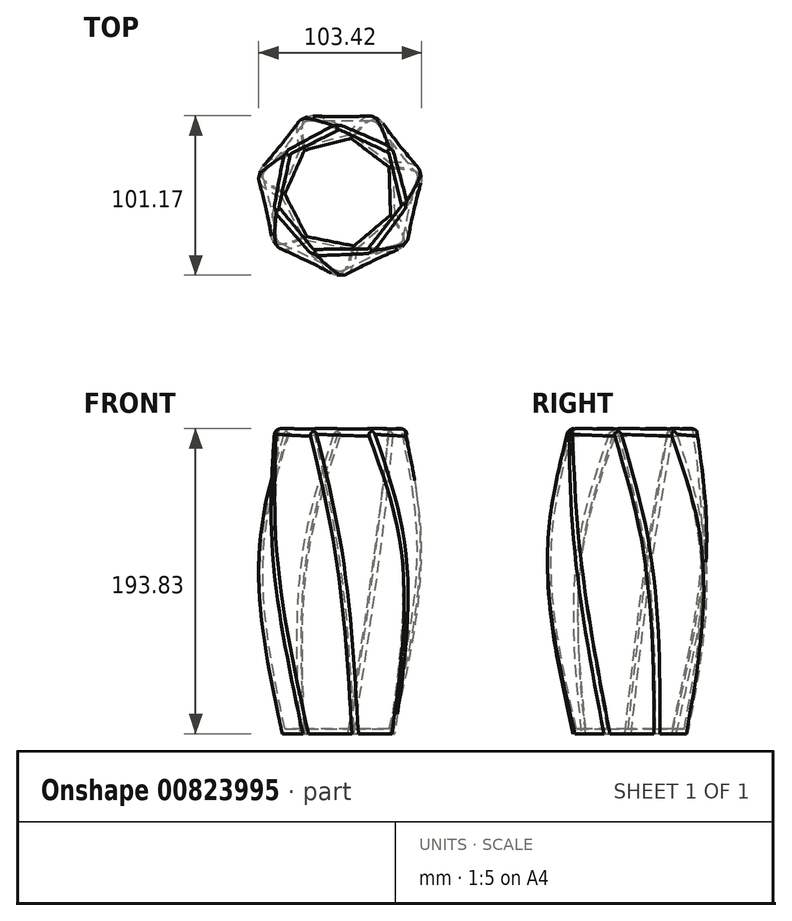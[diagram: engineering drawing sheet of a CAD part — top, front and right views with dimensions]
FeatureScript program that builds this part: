
annotation { "Feature Type Name" : "Feature", "Feature Type Description" : "" }
export const myFeature = defineFeature(function(context is Context, id is Id, definition is map)
    precondition{}
    {
        {
            var Q0;
            Q0=qCreatedBy(makeId("Top.planeOp"),FACE);
            var sketch = newSketch(context, id + "F0", { "sketchPlane" : qUnion([Q0])});
            skCircle(sketch, "E0.cCircle", {"center": v(0, 0) * mm, "radius": 34.1 * mm, "construction": true});
            skLineSegment(sketch, "E0.0", {"start": v(34.68, -15.16) * mm, "end": v(9.77, -36.56) * mm});
            skLineSegment(sketch, "E0.1", {"start": v(9.77, -36.56) * mm, "end": v(-22.5, -30.44) * mm});
            skLineSegment(sketch, "E0.2", {"start": v(-22.5, -30.44) * mm, "end": v(-37.82, -1.4) * mm});
            skLineSegment(sketch, "E0.3", {"start": v(-37.82, -1.4) * mm, "end": v(-24.67, 28.7) * mm});
            skLineSegment(sketch, "E0.4", {"start": v(-24.67, 28.7) * mm, "end": v(7.06, 37.18) * mm});
            skLineSegment(sketch, "E0.5", {"start": v(7.06, 37.18) * mm, "end": v(33.47, 17.66) * mm});
            skLineSegment(sketch, "E0.6", {"start": v(33.47, 17.66) * mm, "end": v(34.68, -15.16) * mm});
            skPoint(sketch, "E0.0.midPoint", {"position": v(22.23, -25.86) * mm});
            skSolve(sketch);
        }
        {
            var Q0;
            Q0=qCreatedBy(makeId("Top.planeOp"),FACE);
            cPlane(context, id + "F1", {"entities" : qUnion([Q0]), "cplaneType" : CPlaneType.OFFSET, "offset" : 127.3 * mm, "width" : 150 * mm, "height" : 150 * mm});
        }
        {
            var Q0;
            Q0=qCreatedBy(id+"F1.planeOp",FACE);
            var sketch = newSketch(context, id + "F2", { "sketchPlane" : qUnion([Q0])});
            skCircle(sketch, "E1.cCircle", {"center": v(0, 0) * mm, "radius": 47.61 * mm, "construction": true});
            skLineSegment(sketch, "E1.0", {"start": v(52.11, 8.77) * mm, "end": v(39.35, -35.27) * mm});
            skLineSegment(sketch, "E1.1", {"start": v(39.35, -35.27) * mm, "end": v(-3.04, -52.76) * mm});
            skLineSegment(sketch, "E1.2", {"start": v(-3.04, -52.76) * mm, "end": v(-43.15, -30.52) * mm});
            skLineSegment(sketch, "E1.3", {"start": v(-43.15, -30.52) * mm, "end": v(-50.76, 14.7) * mm});
            skLineSegment(sketch, "E1.4", {"start": v(-50.76, 14.7) * mm, "end": v(-20.15, 48.85) * mm});
            skLineSegment(sketch, "E1.5", {"start": v(-20.15, 48.85) * mm, "end": v(25.63, 46.21) * mm});
            skLineSegment(sketch, "E1.6", {"start": v(25.63, 46.21) * mm, "end": v(52.11, 8.77) * mm});
            skPoint(sketch, "E1.0.midPoint", {"position": v(45.73, -13.25) * mm});
            skSolve(sketch);
        }
        {
            var Q0;
            Q0=qCreatedBy(id+"F1.planeOp",FACE);
            cPlane(context, id + "F3", {"entities" : qUnion([Q0]), "cplaneType" : CPlaneType.OFFSET, "offset" : 66.6 * mm, "width" : 150 * mm, "height" : 150 * mm});
        }
        {
            var Q0;
            Q0=qCreatedBy(id+"F3.planeOp",FACE);
            var sketch = newSketch(context, id + "F4", { "sketchPlane" : qUnion([Q0])});
            skCircle(sketch, "E2.cCircle", {"center": v(0, 0) * mm, "radius": 38.99 * mm, "construction": true});
            skLineSegment(sketch, "E2.0", {"start": v(42.3, -9.12) * mm, "end": v(19.25, -38.75) * mm});
            skLineSegment(sketch, "E2.1", {"start": v(19.25, -38.75) * mm, "end": v(-18.3, -39.21) * mm});
            skLineSegment(sketch, "E2.2", {"start": v(-18.3, -39.21) * mm, "end": v(-42.07, -10.14) * mm});
            skLineSegment(sketch, "E2.3", {"start": v(-42.07, -10.14) * mm, "end": v(-34.16, 26.57) * mm});
            skLineSegment(sketch, "E2.4", {"start": v(-34.16, 26.57) * mm, "end": v(-0.53, 43.27) * mm});
            skLineSegment(sketch, "E2.5", {"start": v(-0.53, 43.27) * mm, "end": v(33.5, 27.39) * mm});
            skLineSegment(sketch, "E2.6", {"start": v(33.5, 27.39) * mm, "end": v(42.3, -9.12) * mm});
            skPoint(sketch, "E2.0.midPoint", {"position": v(30.77, -23.93) * mm});
            skSolve(sketch);
        }
        {
            var Q0;
            Q0=makeQuery(id+"F0.imprint","IMPRINT",FACE,{"disambiguationData":[TD([[makeQuery(id+"F0.imprint","IMPRINT",EDGE,{"derivedFrom":sQuery(id+"F0.wireOp",EDGE,"E0.0")}),-1.0]])]});
            var Q1;
            Q1=makeQuery(id+"F2.imprint","IMPRINT",FACE,{"disambiguationData":[TD([[makeQuery(id+"F2.imprint","IMPRINT",EDGE,{"derivedFrom":sQuery(id+"F2.wireOp",EDGE,"E1.0")}),-1.0]])]});
            var Q2;
            Q2=makeQuery(id+"F4.imprint","IMPRINT",FACE,{"disambiguationData":[TD([[makeQuery(id+"F4.imprint","IMPRINT",EDGE,{"derivedFrom":sQuery(id+"F4.wireOp",EDGE,"E2.0")}),-1.0]])]});
            loft(context, id + "F5", {"sheetProfilesArray" : [{ "sheetProfileEntities" : qUnion([Q0]) }, { "sheetProfileEntities" : qUnion([Q1]) }, { "sheetProfileEntities" : qUnion([Q2]) }]});
        }
        {
            var Q0;
            Q0=makeQuery(id+"F5.opLoft","CAP_FACE",FACE,{"disambiguationData":[OSD([makeQuery(id+"F4.imprint","IMPRINT",FACE,{"disambiguationData":[TD([[makeQuery(id+"F4.imprint","IMPRINT",EDGE,{"derivedFrom":sQuery(id+"F4.wireOp",EDGE,"E2.0")}),-1.0]])]})])],"isStart":true});
            shell(context, id + "F6", {"entities" : qUnion([Q0]), "thickness" : 3 * mm});
        }
        {
            var Q0;
            Q0=makeQuery(id+"F5.opLoft","SWEPT_EDGE",EDGE,{"disambiguationData":[OSD([sQuery(id+"F0.wireOp",EDGE,"E0.2"),sQuery(id+"F0.wireOp",EDGE,"E0.3"),sQuery(id+"F2.wireOp",EDGE,"E1.3"),sQuery(id+"F2.wireOp",EDGE,"E1.4")])]});
            var Q1;
            Q1=makeQuery(id+"F5.opLoft","SWEPT_EDGE",EDGE,{"disambiguationData":[OSD([sQuery(id+"F0.wireOp",EDGE,"E0.1"),sQuery(id+"F0.wireOp",EDGE,"E0.2"),sQuery(id+"F2.wireOp",EDGE,"E1.2"),sQuery(id+"F2.wireOp",EDGE,"E1.3")])]});
            var Q2;
            Q2=makeQuery(id+"F5.opLoft","SWEPT_EDGE",EDGE,{"disambiguationData":[OSD([sQuery(id+"F0.wireOp",EDGE,"E0.3"),sQuery(id+"F0.wireOp",EDGE,"E0.4"),sQuery(id+"F2.wireOp",EDGE,"E1.4"),sQuery(id+"F2.wireOp",EDGE,"E1.5")])]});
            var Q3;
            Q3=makeQuery(id+"F5.opLoft","SWEPT_EDGE",EDGE,{"disambiguationData":[OSD([sQuery(id+"F0.wireOp",EDGE,"E0.4"),sQuery(id+"F0.wireOp",EDGE,"E0.5"),sQuery(id+"F2.wireOp",EDGE,"E1.5"),sQuery(id+"F2.wireOp",EDGE,"E1.6")])]});
            var Q4;
            Q4=makeQuery(id+"F5.opLoft","SWEPT_EDGE",EDGE,{"disambiguationData":[OSD([sQuery(id+"F0.wireOp",EDGE,"E0.5"),sQuery(id+"F0.wireOp",EDGE,"E0.6"),sQuery(id+"F2.wireOp",EDGE,"E1.0"),sQuery(id+"F2.wireOp",EDGE,"E1.6")])]});
            var Q5;
            Q5=makeQuery(id+"F5.opLoft","SWEPT_EDGE",EDGE,{"disambiguationData":[OSD([sQuery(id+"F0.wireOp",EDGE,"E0.0"),sQuery(id+"F0.wireOp",EDGE,"E0.6"),sQuery(id+"F2.wireOp",EDGE,"E1.0"),sQuery(id+"F2.wireOp",EDGE,"E1.1")])]});
            var Q6;
            Q6=makeQuery(id+"F5.opLoft","SWEPT_EDGE",EDGE,{"disambiguationData":[OSD([sQuery(id+"F0.wireOp",EDGE,"E0.0"),sQuery(id+"F0.wireOp",EDGE,"E0.1"),sQuery(id+"F2.wireOp",EDGE,"E1.1"),sQuery(id+"F2.wireOp",EDGE,"E1.2")])]});
            chamfer(context, id + "F7", {"entities" : qUnion([Q0, Q1, Q2, Q3, Q4, Q5, Q6]), "width" : 5 * mm, "tangentPropagation" : true});
        }
        {
            var Q0;
            Q0=makeQuery(id+"F5.opLoft","MID_CAP_EDGE",EDGE,{"disambiguationData":[OSD([sQuery(id+"F4.wireOp",EDGE,"E2.0"),sQuery(id+"F4.wireOp",EDGE,"E2.5"),sQuery(id+"F4.wireOp",EDGE,"E2.6")])],"capPos":2.0});
            var Q1;
            Q1=makeQuery(id+"F5.opLoft","MID_CAP_EDGE",EDGE,{"disambiguationData":[OSD([sQuery(id+"F4.wireOp",EDGE,"E2.4"),sQuery(id+"F4.wireOp",EDGE,"E2.5"),sQuery(id+"F4.wireOp",EDGE,"E2.6")])],"capPos":2.0});
            var Q2;
            Q2=makeQuery(id+"F5.opLoft","MID_CAP_EDGE",EDGE,{"disambiguationData":[OSD([sQuery(id+"F4.wireOp",EDGE,"E2.3"),sQuery(id+"F4.wireOp",EDGE,"E2.4"),sQuery(id+"F4.wireOp",EDGE,"E2.5")])],"capPos":2.0});
            var Q3;
            Q3=makeQuery(id+"F5.opLoft","MID_CAP_EDGE",EDGE,{"disambiguationData":[OSD([sQuery(id+"F4.wireOp",EDGE,"E2.2"),sQuery(id+"F4.wireOp",EDGE,"E2.3"),sQuery(id+"F4.wireOp",EDGE,"E2.4")])],"capPos":2.0});
            var Q4;
            Q4=makeQuery(id+"F5.opLoft","MID_CAP_EDGE",EDGE,{"disambiguationData":[OSD([sQuery(id+"F4.wireOp",EDGE,"E2.1"),sQuery(id+"F4.wireOp",EDGE,"E2.2"),sQuery(id+"F4.wireOp",EDGE,"E2.3")])],"capPos":2.0});
            var Q5;
            Q5=makeQuery(id+"F5.opLoft","MID_CAP_EDGE",EDGE,{"disambiguationData":[OSD([sQuery(id+"F4.wireOp",EDGE,"E2.0"),sQuery(id+"F4.wireOp",EDGE,"E2.1"),sQuery(id+"F4.wireOp",EDGE,"E2.2")])],"capPos":2.0});
            var Q6;
            Q6=makeQuery(id+"F5.opLoft","MID_CAP_EDGE",EDGE,{"disambiguationData":[OSD([sQuery(id+"F4.wireOp",EDGE,"E2.0"),sQuery(id+"F4.wireOp",EDGE,"E2.1"),sQuery(id+"F4.wireOp",EDGE,"E2.6")])],"capPos":2.0});
            fillet(context, id + "F8", {"entities" : qUnion([Q0, Q1, Q2, Q3, Q4, Q5, Q6]), "radius" : 5 * mm, "tangentPropagation" : true, "allowEdgeOverflow" : false});
        }
    });
